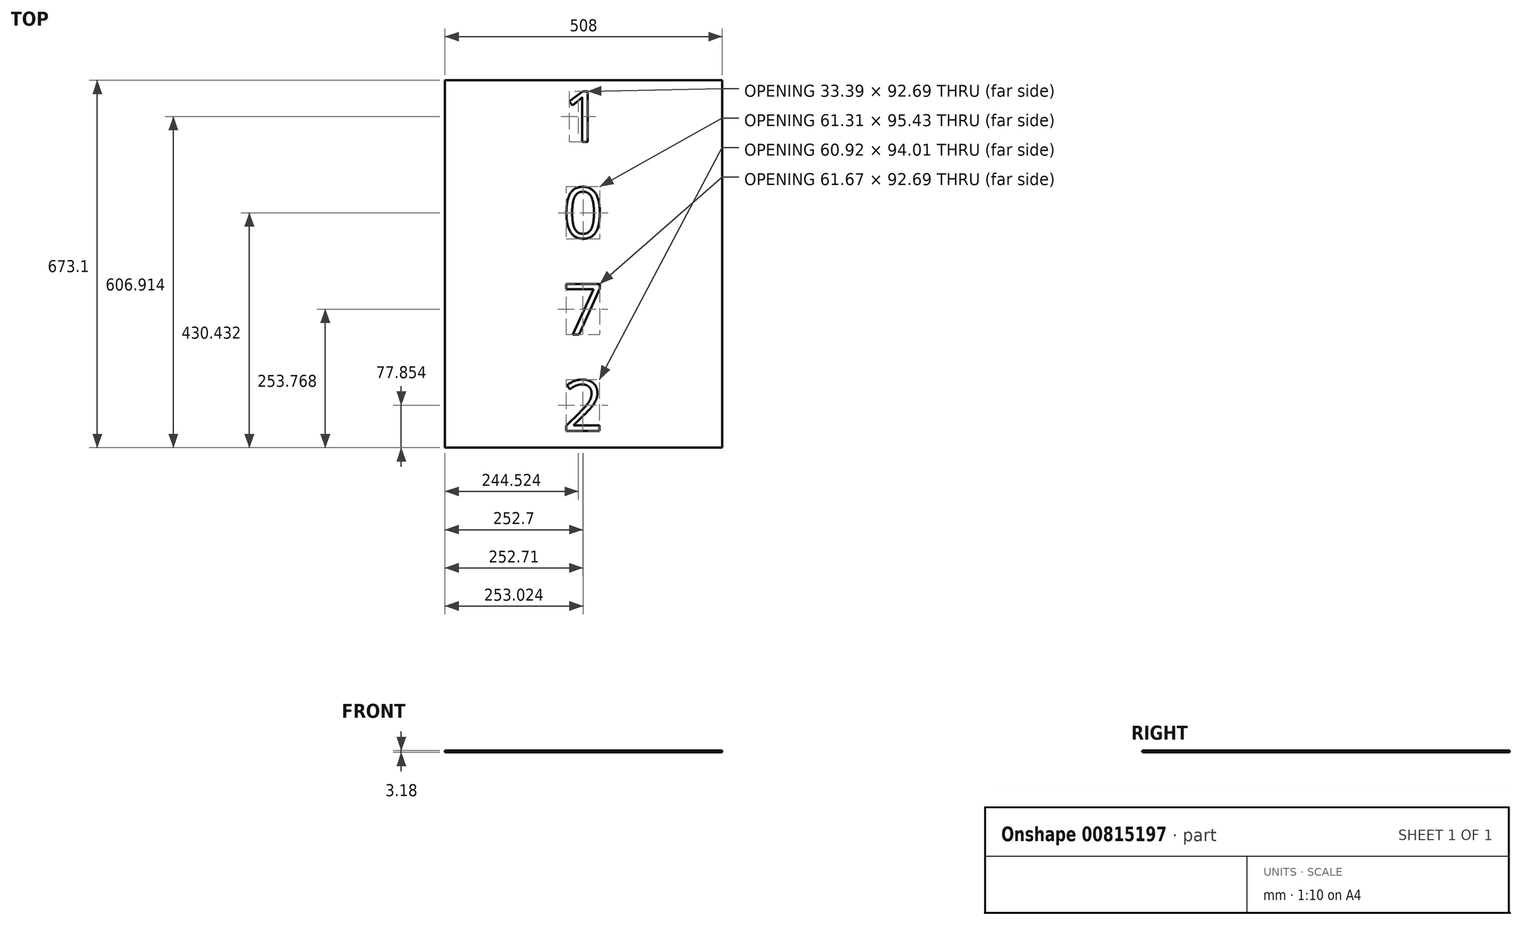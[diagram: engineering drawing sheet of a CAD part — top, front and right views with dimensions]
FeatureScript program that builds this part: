
annotation { "Feature Type Name" : "Feature", "Feature Type Description" : "" }
export const myFeature = defineFeature(function(context is Context, id is Id, definition is map)
    precondition{}
    {
        {
            var Q0;
            Q0=qCreatedBy(makeId("Top.planeOp"),FACE);
            var sketch = newSketch(context, id + "F0", { "sketchPlane" : qUnion([Q0])});
            skLineSegment(sketch, "E0.bottom", {"start": v(0, 0) * mm, "end": v(508, 0) * mm});
            skLineSegment(sketch, "E0.top", {"start": v(0, -673.1) * mm, "end": v(508, -673.1) * mm});
            skLineSegment(sketch, "E0.left", {"start": v(0, 0) * mm, "end": v(0, -673.1) * mm});
            skLineSegment(sketch, "E0.right", {"start": v(508, 0) * mm, "end": v(508, -673.1) * mm});
            skText(sketch, "E1", { "text": "1\n0\n7\n2", "fontName": "OpenSans-Regular.ttf"});
            const initialGuessF0  = {"E1": [0.2159, -0.11253, 1, 0, 0.09348]};
            skSetInitialGuess(sketch, initialGuessF0);
            skSolve(sketch);
        }
        {
            var Q0;
            Q0=makeQuery(id+"F0.imprint","IMPRINT",FACE,{"disambiguationData":[TD([[makeQuery(id+"F0.imprint","IMPRINT",EDGE,{"derivedFrom":sQuery(id+"F0.wireOp",EDGE,"E0.bottom")}),-1.0]])]});
            var Q1;
            Q1=makeQuery(id+"F0.imprint","IMPRINT",FACE,{"disambiguationData":[TD([[makeQuery(id+"F0.imprint","IMPRINT",EDGE,{"derivedFrom":sQuery(id+"F0.wireOp",EDGE,"f2f3c225-0ae4-4d90-aa73-9a4ad0dcf39a.sketch_text.stroke-17")}),1.0]])]});
            var Q2;
            Q2=makeQuery(id+"F0.imprint","IMPRINT",FACE,{"disambiguationData":[TD([[makeQuery(id+"F0.imprint","IMPRINT",EDGE,{"derivedFrom":sQuery(id+"F0.wireOp",EDGE,"b237187f-b3fa-4f5f-893c-b8d83412f774.sketch_text.stroke-17")}),1.0]])]});
            var Q3;
            Q3=makeQuery(id+"F0.imprint","IMPRINT",FACE,{"disambiguationData":[TD([[makeQuery(id+"F0.imprint","IMPRINT",EDGE,{"derivedFrom":sQuery(id+"F0.wireOp",EDGE,"E1.sketch_text.stroke-17")}),1.0]])]});
            extrude(context, id + "F1", {"entities" : qUnion([Q0, Q1, Q2, Q3]), "depth" : 3.17 * mm, "offsetDistance" : 25.4 * mm});
        }
    });
